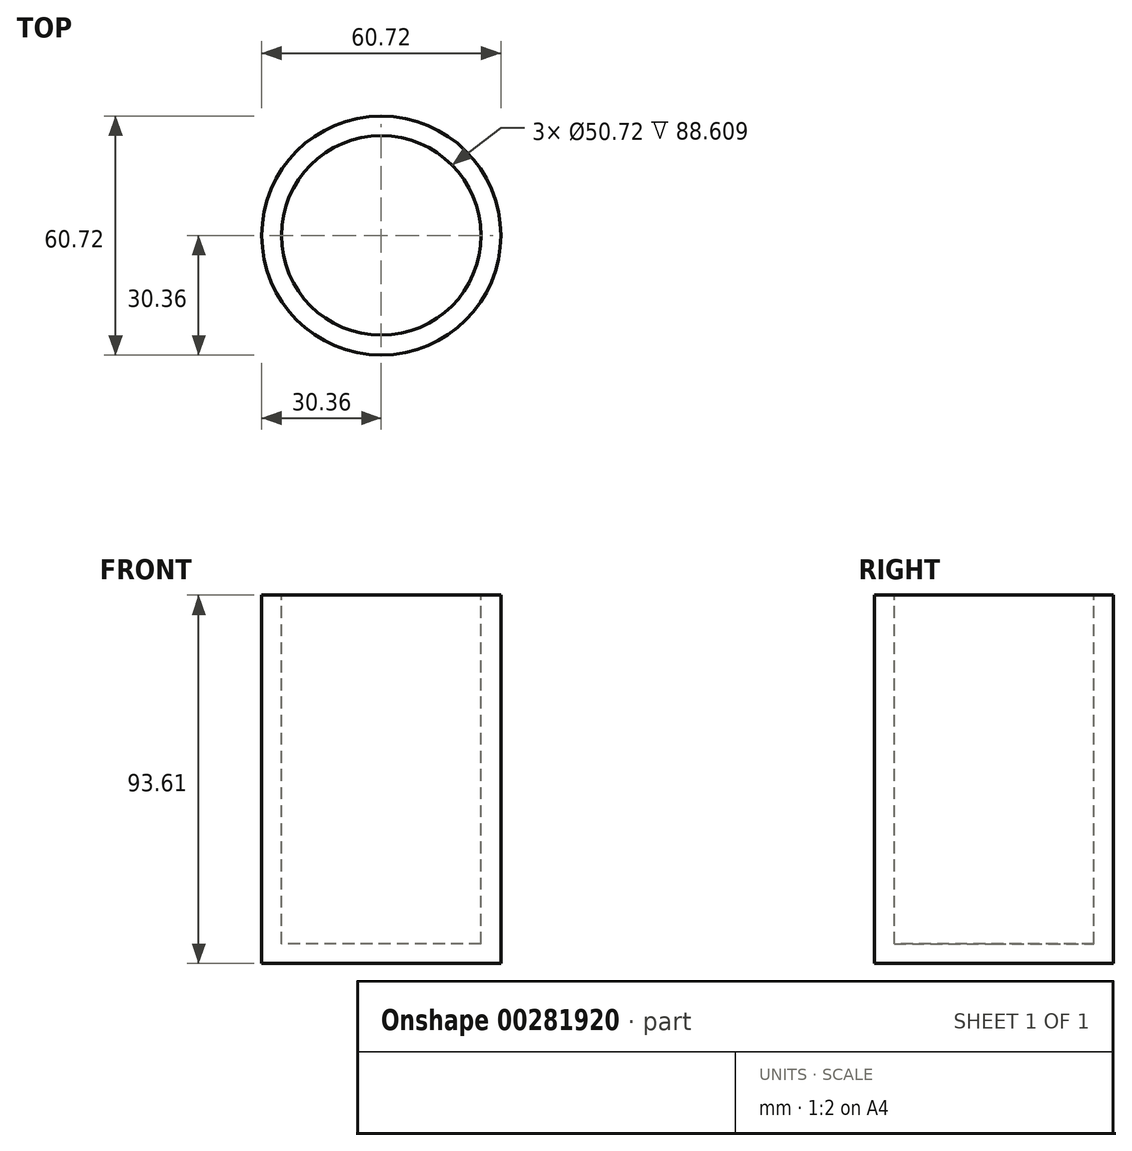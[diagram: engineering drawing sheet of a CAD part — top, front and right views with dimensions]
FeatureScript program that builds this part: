
annotation { "Feature Type Name" : "Feature", "Feature Type Description" : "" }
export const myFeature = defineFeature(function(context is Context, id is Id, definition is map)
    precondition{}
    {
        {
            var Q0;
            Q0=qCreatedBy(makeId("Front.planeOp"),FACE);
            var sketch = newSketch(context, id + "F0", { "sketchPlane" : qUnion([Q0])});
            skLineSegment(sketch, "E0.bottom", {"start": v(25.36, -46.5) * mm, "end": v(-25.36, -46.5) * mm});
            skLineSegment(sketch, "E0.top", {"start": v(25.36, 42.12) * mm, "end": v(-25.36, 42.12) * mm});
            skLineSegment(sketch, "E0.left", {"start": v(25.36, -46.5) * mm, "end": v(25.36, 42.12) * mm});
            skLineSegment(sketch, "E0.right", {"start": v(-25.36, -46.5) * mm, "end": v(-25.36, 42.12) * mm});
            skPoint(sketch, "E0.middle", {"position": v(0, -2.19) * mm});
            skLineSegment(sketch, "E1", {"start": v(0, 42.12) * mm, "end": v(0, -46.5) * mm});
            skSolve(sketch);
        }
        {
            var Q0;
            {var subQ0=sQuery(id+"F0.wireOp",EDGE,"E0.right");Q0=makeQuery(id+"F0.imprint","IMPRINT",FACE,{"disambiguationData":[TD([[makeQuery(id+"F0.imprint","IMPRINT",EDGE,{"derivedFrom":subQ0}),-1.0]])]});}
            var Q1;
            Q1=sQuery(id+"F0.wireOp",EDGE,"E1");
            revolve(context, id + "F1", {"entities" : qUnion([Q0]), "axis" : qUnion([Q1]), "revolveType" : RevolveType.FULL});
        }
        {
            var Q0;
            Q0=makeQuery(id+"F1.opRevolve","SWEPT_FACE",FACE,{"disambiguationData":[OSD([sQuery(id+"F0.wireOp",EDGE,"E0.top")])]});
            shell(context, id + "F2", {"entities" : qUnion([Q0]), "thickness" : 5 * mm, "oppositeDirection" : true});
        }
    });
